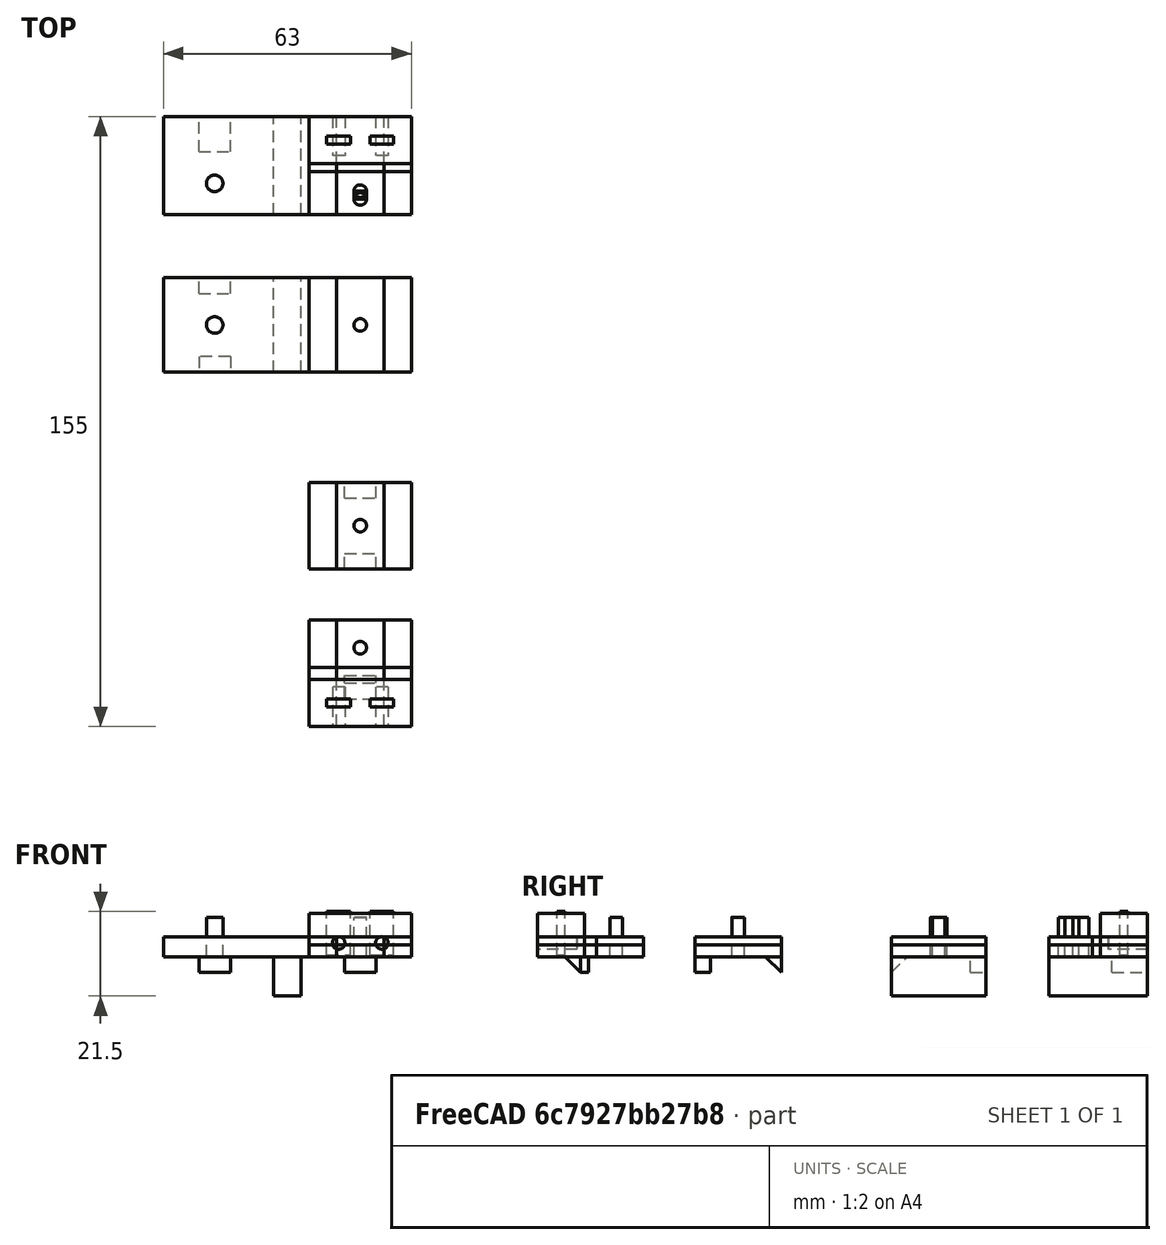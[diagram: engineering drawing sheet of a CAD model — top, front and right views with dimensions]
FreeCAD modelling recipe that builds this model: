
FCSTD DOCUMENT  (FreeCAD 0.18R14555 (Git shallow))
Label: rail-head
License: All rights reserved
LicenseURL: http://en.wikipedia.org/wiki/All_rights_reserved
objects: Part::Box×29, Part::Cylinder×11, App::DocumentObjectGroup×4, Part::Feature×3
note: 43 computed .brp shape members not serialized (recipe doc carries the construction recipe); baked Part::Feature solids carry a one-line shape summary decoded from their .brp

FEATURE [Part::Cylinder] Cylinder  label="drill-hole-1"
  Angle = 360
  AttacherType = Attacher::AttachEngine3D
  Height = 10
  Placement = pos=(-5.5,10,3.5) rot=(1,0,0;1.5708rad)
  Radius = 1.6
FEATURE [Part::Cylinder] Cylinder001  label="drill-hole-2"
  Angle = 360
  AttacherType = Attacher::AttachEngine3D
  Height = 10
  Placement = pos=(5.5,10,3.5) rot=(1,0,0;1.5708rad)
  Radius = 1.6
FEATURE [Part::Box] Box  label="bolt-stopper"
  AttacherType = Attacher::AttachEngine3D
  Height = 4
  Length = 8
  Placement = pos=(-4,11,-4) rot=(0,0,1;0rad)
  Width = 2
FEATURE [Part::Box] Box001  label="square-nut-1"
  AttacherType = Attacher::AttachEngine3D
  Height = 11
  Length = 6
  Placement = pos=(-8.5,5,0.5) rot=(0,0,1;0rad)
  Width = 2
FEATURE [Part::Box] Box002  label="square-nut-2"
  AttacherType = Attacher::AttachEngine3D
  Height = 11
  Length = 6
  Placement = pos=(2.5,5,0.5) rot=(0,0,1;0rad)
  Width = 2
FEATURE [Part::Box] Box003  label="base"
  AttacherType = Attacher::AttachEngine3D
  Height = 3
  Length = 26
  Placement = pos=(-13,0,0) rot=(0,0,1;0rad)
  Width = 27
FEATURE [Part::Cylinder] Cylinder002  label="rail-bolt"
  Angle = 360
  AttacherType = Attacher::AttachEngine3D
  Height = 10
  Placement = pos=(0,20,0) rot=(0,0,1;0rad)
  Radius = 1.6
FEATURE [Part::Box] Box004  label="rail-side-1"
  AttacherType = Attacher::AttachEngine3D
  Height = 5
  Length = 7
  Placement = pos=(-13,0,0) rot=(0,0,1;0rad)
  Width = 27
FEATURE [Part::Box] Box005  label="rail-side-2"
  AttacherType = Attacher::AttachEngine3D
  Height = 5
  Length = 7
  Placement = pos=(6,0,0) rot=(0,0,1;0rad)
  Width = 27
FEATURE [Part::Box] Box006  label="head-stopper"
  AttacherType = Attacher::AttachEngine3D
  Height = 11
  Length = 26
  Placement = pos=(-13,0,0) rot=(0,0,1;0rad)
  Width = 12
FEATURE [Part::Box] Box007  label="head-slot"
  AttacherType = Attacher::AttachEngine3D
  Height = 5
  Length = 26
  Placement = pos=(-13,0,0) rot=(0,0,1;0rad)
  Width = 15
FEATURE [Part::Cylinder] Cylinder003  label="rail-bolt001"
  Angle = 360
  AttacherType = Attacher::AttachEngine3D
  Height = 10
  Placement = pos=(0,51,0) rot=(0,0,1;0rad)
  Radius = 1.6
FEATURE [Part::Box] Box008  label="rail-side-003"
  AttacherType = Attacher::AttachEngine3D
  Height = 5
  Length = 7
  Placement = pos=(-13,40,0) rot=(0,0,1;0rad)
  Width = 22
FEATURE [Part::Box] Box009  label="rail-side-004"
  AttacherType = Attacher::AttachEngine3D
  Height = 5
  Length = 7
  Placement = pos=(6,40,0) rot=(0,0,1;0rad)
  Width = 22
FEATURE [Part::Box] Box010  label="base001"
  AttacherType = Attacher::AttachEngine3D
  Height = 3
  Length = 26
  Placement = pos=(-13,40,0) rot=(0,0,1;0rad)
  Width = 22
FEATURE [Part::Box] Box011  label="bolt-stopper001"
  AttacherType = Attacher::AttachEngine3D
  Height = 4
  Length = 8
  Placement = pos=(-4,40,-4) rot=(0,0,1;0rad)
  Width = 4
FEATURE [Part::Box] Box012  label="rail-side-005"
  AttacherType = Attacher::AttachEngine3D
  Height = 5
  Length = 7
  Placement = pos=(6,130,0) rot=(0,0,1;0rad)
  Width = 25
FEATURE [Part::Box] Box013  label="base002"
  AttacherType = Attacher::AttachEngine3D
  Height = 3
  Length = 26
  Placement = pos=(-13,130,0) rot=(0,0,1;0rad)
  Width = 25
FEATURE [Part::Box] Box015  label="rail-side-006"
  AttacherType = Attacher::AttachEngine3D
  Height = 5
  Length = 7
  Placement = pos=(-13,130,0) rot=(0,0,1;0rad)
  Width = 25
FEATURE [Part::Box] Box016  label="head-stopper001"
  AttacherType = Attacher::AttachEngine3D
  Height = 11
  Length = 26
  Placement = pos=(-13,143,0) rot=(0,0,1;0rad)
  Width = 12
FEATURE [Part::Feature] Body006  label="45-slope004"
  Placement = pos=(-4,11,4) rot=(0,0,1;0rad)
  shape: bbox 8 x 4 x 4 mm, 5 faces (baked)
FEATURE [App::DocumentObjectGroup] Group  label="head"
  Group = -> [Cylinder,Cylinder001,Box,Box001,Box002,Box003,Cylinder002,Box004,Box005,Box006,Box007,Body006]
FEATURE [Part::Box] Box017  label="tail-slot001"
  AttacherType = Attacher::AttachEngine3D
  Height = 5
  Length = 26
  Placement = pos=(-13,141,0) rot=(0,0,1;0rad)
  Width = 14
FEATURE [Part::Cylinder] Cylinder007  label="rail-bolt005"
  Angle = 360
  AttacherType = Attacher::AttachEngine3D
  Height = 10
  Placement = pos=(0,134,0) rot=(0,0,1;0rad)
  Radius = 1.6
FEATURE [Part::Cylinder] Cylinder008  label="rail-bolt006"
  Angle = 360
  AttacherType = Attacher::AttachEngine3D
  Height = 10
  Placement = pos=(0,136,0) rot=(0,0,1;0rad)
  Radius = 1.6
FEATURE [Part::Box] Box019  label="bolt-play"
  AttacherType = Attacher::AttachEngine3D
  Height = 10
  Length = 3.2
  Placement = pos=(-1.6,134,0) rot=(0,0,1;0rad)
  Width = 2
FEATURE [Part::Box] Box025  label="ref-spacer002"
  AttacherType = Attacher::AttachEngine3D
  Height = 5
  Length = 37
  Placement = pos=(-50,130,0) rot=(0,0,1;0rad)
  Width = 25
FEATURE [Part::Box] Box026  label="Cube001"
  AttacherType = Attacher::AttachEngine3D
  Height = 4
  Length = 8
  Placement = pos=(-41,146,-4) rot=(0,0,1;0rad)
  Width = 9
FEATURE [Part::Cylinder] Cylinder012  label="drill-hole-005"
  Angle = 360
  AttacherType = Attacher::AttachEngine3D
  Height = 10
  Placement = pos=(-5.5,155,3.5) rot=(1,0,0;1.5708rad)
  Radius = 1.6
FEATURE [Part::Box] Box027  label="ref-spacer003"
  AttacherType = Attacher::AttachEngine3D
  Height = 10
  Length = 7
  Placement = pos=(-22,130,-10) rot=(0,0,1;0rad)
  Width = 25
FEATURE [Part::Box] Box028  label="square-nut-005"
  AttacherType = Attacher::AttachEngine3D
  Height = 11
  Length = 6
  Placement = pos=(2.5,148,0.5) rot=(0,0,1;0rad)
  Width = 2
FEATURE [Part::Cylinder] Cylinder013  label="drill-hole-006"
  Angle = 360
  AttacherType = Attacher::AttachEngine3D
  Height = 10
  Placement = pos=(5.5,155,3.5) rot=(1,0,0;1.5708rad)
  Radius = 1.6
FEATURE [Part::Box] Box029  label="square-nut-006"
  AttacherType = Attacher::AttachEngine3D
  Height = 11
  Length = 6
  Placement = pos=(-8.5,148,0.5) rot=(0,0,1;0rad)
  Width = 2
FEATURE [Part::Cylinder] Cylinder014  label="t-slot-bolt001"
  Angle = 360
  AttacherType = Attacher::AttachEngine3D
  Height = 10
  Placement = pos=(-37,138,0) rot=(0,0,1;0rad)
  Radius = 2.1
FEATURE [App::DocumentObjectGroup] Group002  label="tail"
  Group = -> [Box015,Box013,Box012,Box016,Box017,Cylinder007,Cylinder008,Box019,Box025,Cylinder014,Box028,Cylinder013,Cylinder012,Box027,Box029,Box026]
FEATURE [Part::Box] Box030  label="Cube002"
  AttacherType = Attacher::AttachEngine3D
  Height = 4
  Length = 8
  Placement = pos=(-41,110,-4) rot=(0,0,1;0rad)
  Width = 4
FEATURE [Part::Box] Box031  label="rail-side-007"
  AttacherType = Attacher::AttachEngine3D
  Height = 5
  Length = 7
  Placement = pos=(-13,90,0) rot=(0,0,1;0rad)
  Width = 24
FEATURE [Part::Cylinder] Cylinder015  label="rail-bolt007"
  Angle = 360
  AttacherType = Attacher::AttachEngine3D
  Height = 10
  Placement = pos=(0,102,0) rot=(0,0,1;0rad)
  Radius = 1.6
FEATURE [Part::Box] Box032  label="base003"
  AttacherType = Attacher::AttachEngine3D
  Height = 3
  Length = 26
  Placement = pos=(-13,90,0) rot=(0,0,1;0rad)
  Width = 24
FEATURE [Part::Box] Box033  label="ref-spacer004"
  AttacherType = Attacher::AttachEngine3D
  Height = 5
  Length = 37
  Placement = pos=(-50,90,0) rot=(0,0,1;0rad)
  Width = 24
FEATURE [Part::Cylinder] Cylinder016  label="t-slot-bolt002"
  Angle = 360
  AttacherType = Attacher::AttachEngine3D
  Height = 10
  Placement = pos=(-37,102,0) rot=(0,0,1;0rad)
  Radius = 2.1
FEATURE [Part::Box] Box035  label="rail-side-008"
  AttacherType = Attacher::AttachEngine3D
  Height = 5
  Length = 7
  Placement = pos=(6,90,0) rot=(0,0,1;0rad)
  Width = 24
FEATURE [Part::Box] Box037  label="ref-spacer005"
  AttacherType = Attacher::AttachEngine3D
  Height = 10
  Length = 7
  Placement = pos=(-22,90,-10) rot=(0,0,1;0rad)
  Width = 24
FEATURE [Part::Feature] Body007  label="45-slope005"
  Placement = pos=(-33,90,4) rot=(0,0,1;3.14159rad)
  shape: bbox 8 x 4 x 4 mm, 5 faces (baked)
FEATURE [App::DocumentObjectGroup] Group003  label="node-bridge"
  Group = -> [Box032,Box037,Cylinder015,Box030,Cylinder016,Box033,Box035,Box031,Body007]
FEATURE [Part::Feature] Body008  label="45-slope006"
  Placement = pos=(-4,62,4) rot=(0,0,1;0rad)
  shape: bbox 8 x 4 x 4 mm, 5 faces (baked)
FEATURE [App::DocumentObjectGroup] Group001  label="node"
  Group = -> [Box009,Box010,Box011,Box008,Cylinder003,Body008]
